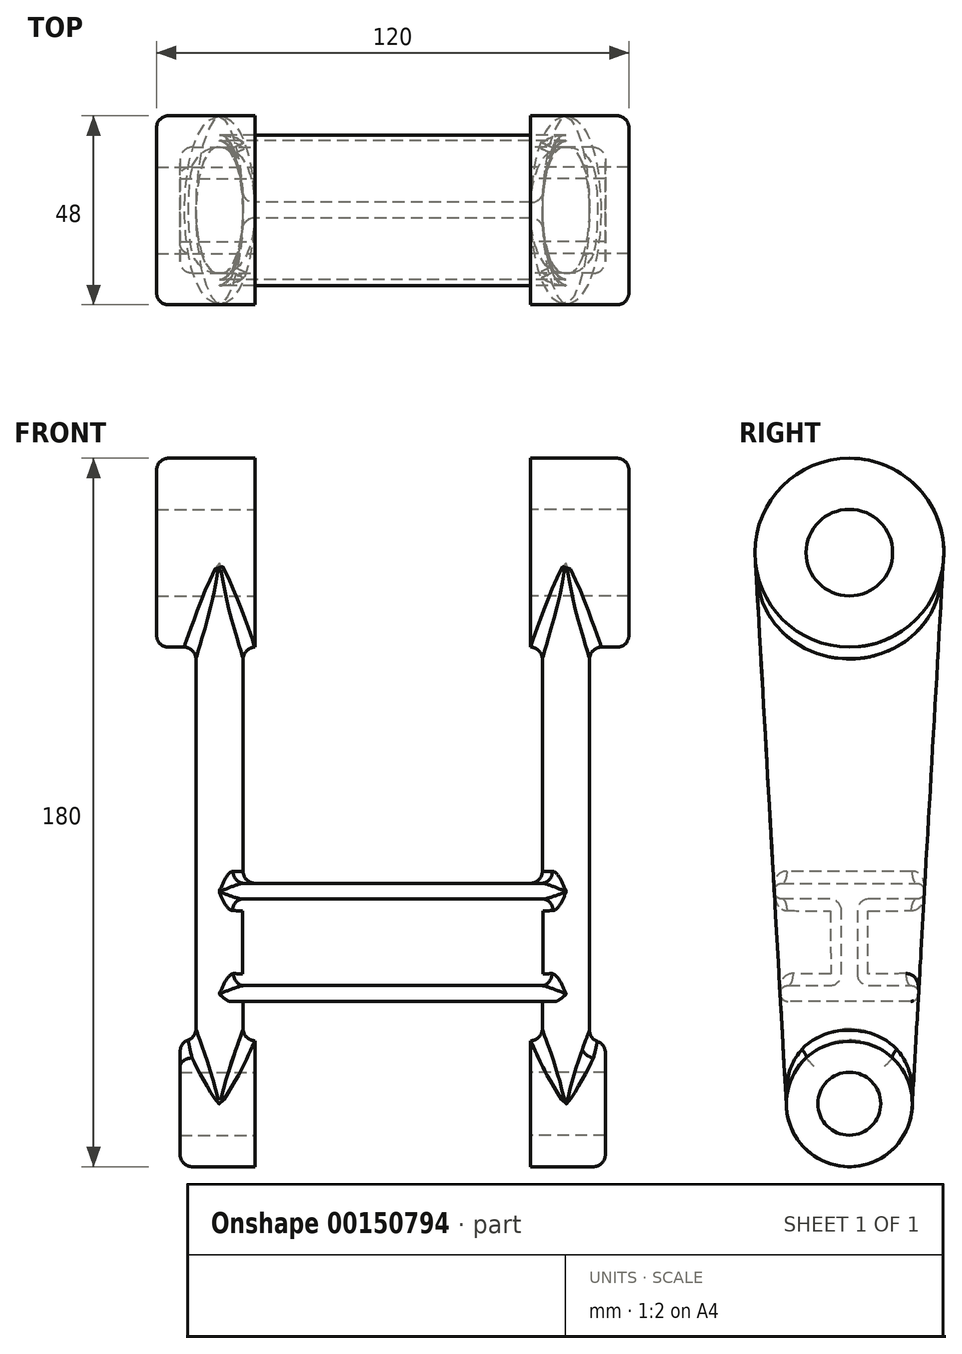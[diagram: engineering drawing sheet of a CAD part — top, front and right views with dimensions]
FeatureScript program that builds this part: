
annotation { "Feature Type Name" : "Feature", "Feature Type Description" : "" }
export const myFeature = defineFeature(function(context is Context, id is Id, definition is map)
    precondition{}
    {
        {
            assignVariable(context, id + "F0", {"name" : "gap", "anyValue" : 70 * mm});
        }
        {
            var Q0;
            Q0=qCreatedBy(makeId("Right.planeOp"),FACE);
            var sketch = newSketch(context, id + "F1", { "sketchPlane" : qUnion([Q0])});
            skCircle(sketch, "E0", {"center": v(0, 0) * mm, "radius": 8 * mm});
            skCircle(sketch, "E1", {"center": v(0, 0) * mm, "radius": 16 * mm});
            skCircle(sketch, "E2", {"center": v(0, 140) * mm, "radius": 11 * mm});
            skCircle(sketch, "E3", {"center": v(0, 140) * mm, "radius": 24 * mm});
            skSolve(sketch);
        }
        {
            var Q0;
            Q0=makeQuery(id+"F1.imprint","IMPRINT",FACE,{"disambiguationData":[TD([[makeQuery(id+"F1.imprint","IMPRINT",EDGE,{"derivedFrom":sQuery(id+"F1.wireOp",EDGE,"E0")}),1.0]])]});
            var Q1;
            Q1=makeQuery(id+"F1.imprint","IMPRINT",FACE,{"disambiguationData":[TD([[makeQuery(id+"F1.imprint","IMPRINT",EDGE,{"derivedFrom":sQuery(id+"F1.wireOp",EDGE,"E0")}),-1.0]])]});
            extrude(context, id + "F2", {"entities" : qUnion([Q0, Q1]), "depth" : 19 * mm});
        }
        {
            var Q0;
            Q0=makeQuery(id+"F1.imprint","IMPRINT",FACE,{"disambiguationData":[TD([[makeQuery(id+"F1.imprint","IMPRINT",EDGE,{"derivedFrom":sQuery(id+"F1.wireOp",EDGE,"E2")}),1.0]])]});
            var Q1;
            Q1=makeQuery(id+"F1.imprint","IMPRINT",FACE,{"disambiguationData":[TD([[makeQuery(id+"F1.imprint","IMPRINT",EDGE,{"derivedFrom":sQuery(id+"F1.wireOp",EDGE,"E2")}),-1.0]])]});
            extrude(context, id + "F3", {"entities" : qUnion([Q0, Q1]), "depth" : 25 * mm});
        }
        {
            var Q0;
            Q0=qCreatedBy(makeId("Top.planeOp"),FACE);
            var sketch = newSketch(context, id + "F4", { "sketchPlane" : qUnion([Q0])});
            skEllipse(sketch, "E4", {"center": v(9, 0) * mm, "majorRadius": 16 * mm, "minorRadius": 6 * mm, "majorAxis": v(0, -1)});
            skPoint(sketch, "E5", {"position": v(3, 0) * mm});
            skLineSegment(sketch, "E6", {"start": v(0, 16) * mm, "end": v(19, 16) * mm, "construction": true});
            skSolve(sketch);
        }
        {
            var Q0;
            Q0=sQuery(id+"F1.wireOp",VERTEX,"E3.center");
            var Q1;
            Q1=qCreatedBy(makeId("Top.planeOp"),FACE);
            cPlane(context, id + "F5", {"entities" : qUnion([Q0, Q1]), "cplaneType" : CPlaneType.PLANE_POINT, "offset" : 25 * mm, "width" : 150 * mm, "height" : 150 * mm});
        }
        {
            var Q0;
            Q0=qCreatedBy(id+"F5.planeOp",FACE);
            var sketch = newSketch(context, id + "F6", { "sketchPlane" : qUnion([Q0])});
            skEllipse(sketch, "E7", {"center": v(9, 0) * mm, "majorRadius": 24 * mm, "minorRadius": 6 * mm, "majorAxis": v(0, 1)});
            skPoint(sketch, "E8", {"position": v(3, 0) * mm});
            skLineSegment(sketch, "E9", {"start": v(0, 24) * mm, "end": v(25, 24) * mm, "construction": true});
            skSolve(sketch);
        }
        {
            var Q0;
            Q0=makeQuery(id+"F6.imprint","IMPRINT",FACE,{"disambiguationData":[TD([[makeQuery(id+"F6.imprint","IMPRINT",EDGE,{"derivedFrom":sQuery(id+"F6.wireOp",EDGE,"E7")}),1.0]])]});
            var Q1;
            Q1=makeQuery(id+"F4.imprint","IMPRINT",FACE,{"disambiguationData":[TD([[makeQuery(id+"F4.imprint","IMPRINT",EDGE,{"derivedFrom":sQuery(id+"F4.wireOp",EDGE,"E4")}),1.0]])]});
            loft(context, id + "F7", {"operationType" : NewBodyOperationType.ADD, "sheetProfilesArray" : [{ "sheetProfileEntities" : qUnion([Q0]) }, { "sheetProfileEntities" : qUnion([Q1]) }]});
        }
        {
            var Q0;
            Q0=makeQuery(id+"F1.imprint","IMPRINT",FACE,{"disambiguationData":[TD([[makeQuery(id+"F1.imprint","IMPRINT",EDGE,{"derivedFrom":sQuery(id+"F1.wireOp",EDGE,"E2")}),1.0]])]});
            var Q1;
            Q1=makeQuery(id+"F1.imprint","IMPRINT",FACE,{"disambiguationData":[TD([[makeQuery(id+"F1.imprint","IMPRINT",EDGE,{"derivedFrom":sQuery(id+"F1.wireOp",EDGE,"E0")}),1.0]])]});
            extrude(context, id + "F8", {"entities" : qUnion([Q0, Q1]), "operationType" : NewBodyOperationType.REMOVE, "depth" : 25 * mm});
        }
        {
            var Q0;
            Q0=sQuery(id+"F4.wireOp",VERTEX,"E4.center");
            var Q1;
            Q1=qCreatedBy(makeId("Right.planeOp"),FACE);
            cPlane(context, id + "F9", {"entities" : qUnion([Q0, Q1]), "cplaneType" : CPlaneType.PLANE_POINT, "offset" : 25 * mm, "width" : 150 * mm, "height" : 150 * mm});
        }
        {
            var Q0;
            Q0=qCreatedBy(makeId("Right.planeOp"),FACE);
            cPlane(context, id + "F10", {"entities" : qUnion([Q0]), "cplaneType" : CPlaneType.OFFSET, "offset" : getVariable(context, 'gap') / 2, "oppositeDirection" : true, "width" : 150 * mm, "height" : 150 * mm});
        }
        {
            var Q0;
            Q0=makeQuery(id+"F2.opExtrude","SWEPT_BODY",BODY,{"disambiguationData":[OSD([sQuery(id+"F1.wireOp",EDGE,"E1")])]});
            var Q1;
            Q1=qCreatedBy(id+"F10.planeOp",FACE);
            mirror(context, id + "F11", {"entities" : qUnion([Q0]), "mirrorPlane" : qUnion([Q1])});
        }
        {
            var Q0;
            Q0=qCreatedBy(makeId("Right.planeOp"),FACE);
            var sketch = newSketch(context, id + "F12", { "sketchPlane" : qUnion([Q0])});
            skLineSegment(sketch, "E10", {"start": v(23.96, 138.63) * mm, "end": v(15.97, -0.91) * mm, "construction": true});
            skLineSegment(sketch, "E11", {"start": v(17.51, 26) * mm, "end": v(-15.6, 26) * mm});
            skLineSegment(sketch, "E12", {"start": v(-15.6, 26) * mm, "end": v(-15.6, 30) * mm, "construction": true});
            skLineSegment(sketch, "E13", {"start": v(-15.6, 30) * mm, "end": v(-5, 30) * mm});
            skLineSegment(sketch, "E14", {"start": v(-2, 33) * mm, "end": v(-2, 49) * mm});
            skLineSegment(sketch, "E15", {"start": v(-5, 52) * mm, "end": v(-17.1, 52) * mm});
            skLineSegment(sketch, "E16", {"start": v(-17.1, 52) * mm, "end": v(-17.1, 56) * mm, "construction": true});
            skLineSegment(sketch, "E17", {"start": v(-17.1, 56) * mm, "end": v(17.11, 56) * mm});
            skLineSegment(sketch, "E18", {"start": v(17.11, 52) * mm, "end": v(5, 52) * mm});
            skLineSegment(sketch, "E19", {"start": v(2, 49) * mm, "end": v(2, 33) * mm});
            skLineSegment(sketch, "E20", {"start": v(5, 30) * mm, "end": v(17.74, 30) * mm});
            skLineSegment(sketch, "E21", {"start": v(15.63, 30) * mm, "end": v(15.63, 26) * mm, "construction": true});
            skLineSegment(sketch, "E22", {"start": v(-23.96, 138.62) * mm, "end": v(-16, 0) * mm, "construction": true});
            skPoint(sketch, "E23.visualSharp", {"position": v(0, 52) * mm});
            skArc(sketch, "E23.filletArc", {"start": v(5, 52) * mm, "mid": v(2.88, 51.12) * mm, "end": v(2, 49) * mm});
            skPoint(sketch, "E24.visualSharp", {"position": v(-2, 52) * mm});
            skArc(sketch, "E24.filletArc", {"start": v(-2, 49) * mm, "mid": v(-2.88, 51.12) * mm, "end": v(-5, 52) * mm});
            skPoint(sketch, "E25.visualSharp", {"position": v(-2, 30) * mm});
            skArc(sketch, "E25.filletArc", {"start": v(-5, 30) * mm, "mid": v(-2.88, 30.88) * mm, "end": v(-2, 33) * mm});
            skPoint(sketch, "E26.visualSharp", {"position": v(2, 30) * mm});
            skArc(sketch, "E26.filletArc", {"start": v(2, 33) * mm, "mid": v(2.88, 30.88) * mm, "end": v(5, 30) * mm});
            skPoint(sketch, "E27.endSnap0", {"position": v(0, 56) * mm});
            skLineSegment(sketch, "E28", {"start": v(0, 0) * mm, "end": v(0, 93.69) * mm, "construction": true});
            skArc(sketch, "E29", {"start": v(-15.6, 30) * mm, "mid": v(-17.6, 28) * mm, "end": v(-15.6, 26) * mm});
            skArc(sketch, "E30", {"start": v(-17.1, 56) * mm, "mid": v(-19.1, 54) * mm, "end": v(-17.1, 52) * mm});
            skArc(sketch, "E31", {"start": v(17.11, 52) * mm, "mid": v(19.11, 54) * mm, "end": v(17.11, 56) * mm});
            skLineSegment(sketch, "E32", {"start": v(17.11, 52) * mm, "end": v(17.11, 56) * mm, "construction": true});
            skArc(sketch, "E33", {"start": v(15.63, 26) * mm, "mid": v(17.63, 28) * mm, "end": v(15.63, 30) * mm});
            skSolve(sketch);
        }
        {
            var Q0;
            Q0=qSketchRegion(id+"F12",true);
            var Q1;
            Q1=qCreatedBy(id+"F9.planeOp",FACE);
            var Q2;
            Q2=qCreatedBy(id+"F10.planeOp",FACE);
            var Q3;
            Q3=makeQuery(id+"F11.opPattern","COPY",BODY,{"derivedFrom":makeQuery(id+"F2.opExtrude","SWEPT_BODY",BODY,{"disambiguationData":[OSD([sQuery(id+"F1.wireOp",EDGE,"E1")])]}),"instanceName":"1"});
            extrude(context, id + "F13", {"entities" : qUnion([Q0]), "operationType" : NewBodyOperationType.ADD, "endBound" : BoundingType.UP_TO_SURFACE, "endBoundEntityFace" : qUnion([Q1]), "depth" : 30 * mm, "hasSecondDirection" : true, "secondDirectionBound" : SecondDirectionBoundingType.UP_TO_SURFACE, "secondDirectionOppositeDirection" : true, "secondDirectionBoundEntityFace" : qUnion([Q2]), "secondDirectionBoundEntityBody" : qUnion([Q3]), "secondDirectionDepth" : 25 * mm});
        }
        {
            var Q0;
            Q0=makeQuery(id+"F13.boolean.opBoolean","INTERSECT",EDGE,{"derivedFrom":[makeQuery(id+"F7.opLoft","SWEPT_FACE",FACE,{"disambiguationData":[OSD([sQuery(id+"F4.wireOp",EDGE,"E4"),sQuery(id+"F6.wireOp",EDGE,"E7")])]}),makeQuery(id+"F13.opExtrude","SWEPT_FACE",FACE,{"disambiguationData":[OSD([sQuery(id+"F12.wireOp",EDGE,"E17")])]})]});
            fillet(context, id + "F14", {"entities" : qUnion([Q0]), "radius" : 3 * mm, "tangentPropagation" : true, "allowEdgeOverflow" : false});
        }
        {
            var Q0;
            Q0=makeQuery(id+"F13.boolean.opBoolean","INTERSECT",EDGE,{"derivedFrom":[makeQuery(id+"F7.opLoft","SWEPT_FACE",FACE,{"disambiguationData":[OSD([sQuery(id+"F4.wireOp",EDGE,"E4"),sQuery(id+"F6.wireOp",EDGE,"E7")])]}),makeQuery(id+"F13.opExtrude","SWEPT_FACE",FACE,{"disambiguationData":[OSD([sQuery(id+"F12.wireOp",EDGE,"E13")])]})]});
            var Q1;
            Q1=makeQuery(id+"F13.boolean.opBoolean","INTERSECT",EDGE,{"derivedFrom":[makeQuery(id+"F7.opLoft","SWEPT_FACE",FACE,{"disambiguationData":[OSD([sQuery(id+"F4.wireOp",EDGE,"E4"),sQuery(id+"F6.wireOp",EDGE,"E7")])]}),makeQuery(id+"F13.opExtrude","SWEPT_FACE",FACE,{"disambiguationData":[OSD([sQuery(id+"F12.wireOp",EDGE,"E14")])]})]});
            var Q2;
            Q2=makeQuery(id+"F13.boolean.opBoolean","INTERSECT",EDGE,{"derivedFrom":[makeQuery(id+"F7.opLoft","SWEPT_FACE",FACE,{"disambiguationData":[OSD([sQuery(id+"F4.wireOp",EDGE,"E4"),sQuery(id+"F6.wireOp",EDGE,"E7")])]}),makeQuery(id+"F13.opExtrude","SWEPT_FACE",FACE,{"disambiguationData":[OSD([sQuery(id+"F12.wireOp",EDGE,"E20")])]})]});
            var Q3;
            Q3=makeQuery(id+"F13.boolean.opBoolean","INTERSECT",EDGE,{"derivedFrom":[makeQuery(id+"F7.opLoft","SWEPT_FACE",FACE,{"disambiguationData":[OSD([sQuery(id+"F4.wireOp",EDGE,"E4"),sQuery(id+"F6.wireOp",EDGE,"E7")])]}),makeQuery(id+"F13.opExtrude","SWEPT_FACE",FACE,{"disambiguationData":[OSD([sQuery(id+"F12.wireOp",EDGE,"E19")])]})]});
            fillet(context, id + "F15", {"entities" : qUnion([Q0, Q1, Q2, Q3]), "radius" : 3 * mm, "tangentPropagation" : true, "allowEdgeOverflow" : false});
        }
        {
            var Q0;
            Q0=makeQuery(id+"F2.opExtrude","SWEPT_BODY",BODY,{"disambiguationData":[OSD([sQuery(id+"F1.wireOp",EDGE,"E1")])]});
            var Q1;
            Q1=qCreatedBy(id+"F10.planeOp",FACE);
            mirror(context, id + "F16", {"operationType" : NewBodyOperationType.ADD, "entities" : qUnion([Q0]), "mirrorPlane" : qUnion([Q1])});
        }
        {
            var Q0;
            Q0=makeQuery(id+"F3.opExtrude","CAP_EDGE",EDGE,{"disambiguationData":[OSD([sQuery(id+"F1.wireOp",EDGE,"E3")])],"isStart":false});
            var Q1;
            Q1=makeQuery(id+"F16.opPattern","COPY",EDGE,{"derivedFrom":makeQuery(id+"F3.opExtrude","CAP_EDGE",EDGE,{"disambiguationData":[OSD([sQuery(id+"F1.wireOp",EDGE,"E3")])],"isStart":false}),"instanceName":"1"});
            var Q2;
            Q2=makeQuery(id+"F2.opExtrude","CAP_EDGE",EDGE,{"disambiguationData":[OSD([sQuery(id+"F1.wireOp",EDGE,"E1")])],"isStart":false});
            var Q3;
            Q3=makeQuery(id+"F16.opPattern","COPY",EDGE,{"derivedFrom":makeQuery(id+"F2.opExtrude","CAP_EDGE",EDGE,{"disambiguationData":[OSD([sQuery(id+"F1.wireOp",EDGE,"E1")])],"isStart":false}),"instanceName":"1"});
            fillet(context, id + "F17", {"entities" : qUnion([Q0, Q1, Q2, Q3]), "radius" : 3 * mm, "tangentPropagation" : true, "allowEdgeOverflow" : false});
        }
        {
            var Q0;
            Q0=makeQuery(id+"F7.boolean.opBoolean","INTERSECT",EDGE,{"derivedFrom":[makeQuery(id+"F3.opExtrude","SWEPT_FACE",FACE,{"disambiguationData":[OSD([sQuery(id+"F1.wireOp",EDGE,"E3")])]}),makeQuery(id+"F7.opLoft","SWEPT_FACE",FACE,{"disambiguationData":[OSD([sQuery(id+"F4.wireOp",EDGE,"E4"),sQuery(id+"F6.wireOp",EDGE,"E7")])]})]});
            var Q1;
            Q1=makeQuery(id+"F11.opPattern","COPY",EDGE,{"derivedFrom":makeQuery(id+"F7.boolean.opBoolean","INTERSECT",EDGE,{"derivedFrom":[makeQuery(id+"F3.opExtrude","SWEPT_FACE",FACE,{"disambiguationData":[OSD([sQuery(id+"F1.wireOp",EDGE,"E3")])]}),makeQuery(id+"F7.opLoft","SWEPT_FACE",FACE,{"disambiguationData":[OSD([sQuery(id+"F4.wireOp",EDGE,"E4"),sQuery(id+"F6.wireOp",EDGE,"E7")])]})]}),"instanceName":"1"});
            var Q2;
            Q2=makeQuery(id+"F11.opPattern","COPY",EDGE,{"derivedFrom":makeQuery(id+"F7.boolean.opBoolean","INTERSECT",EDGE,{"derivedFrom":[makeQuery(id+"F2.opExtrude","SWEPT_FACE",FACE,{"disambiguationData":[OSD([sQuery(id+"F1.wireOp",EDGE,"E1")])]}),makeQuery(id+"F7.opLoft","SWEPT_FACE",FACE,{"disambiguationData":[OSD([sQuery(id+"F4.wireOp",EDGE,"E4"),sQuery(id+"F6.wireOp",EDGE,"E7")])]})]}),"instanceName":"1"});
            var Q3;
            Q3=makeQuery(id+"F7.boolean.opBoolean","INTERSECT",EDGE,{"derivedFrom":[makeQuery(id+"F2.opExtrude","SWEPT_FACE",FACE,{"disambiguationData":[OSD([sQuery(id+"F1.wireOp",EDGE,"E1")])]}),makeQuery(id+"F7.opLoft","SWEPT_FACE",FACE,{"disambiguationData":[OSD([sQuery(id+"F4.wireOp",EDGE,"E4"),sQuery(id+"F6.wireOp",EDGE,"E7")])]})]});
            fillet(context, id + "F18", {"entities" : qUnion([Q0, Q1, Q2, Q3]), "radius" : 3 * mm, "tangentPropagation" : true, "allowEdgeOverflow" : false});
        }
        {
            var Q0;
            Q0=makeQuery(id+"F11.opPattern","COPY",EDGE,{"derivedFrom":makeQuery(id+"F2.opExtrude","CAP_EDGE",EDGE,{"disambiguationData":[OSD([sQuery(id+"F1.wireOp",EDGE,"E1")])],"isStart":false}),"instanceName":"1"});
            var Q1;
            Q1=makeQuery(id+"F11.opPattern","COPY",EDGE,{"derivedFrom":makeQuery(id+"F3.opExtrude","CAP_EDGE",EDGE,{"disambiguationData":[OSD([sQuery(id+"F1.wireOp",EDGE,"E3")])],"isStart":false}),"instanceName":"1"});
            fillet(context, id + "F19", {"entities" : qUnion([Q0, Q1]), "radius" : 3 * mm, "tangentPropagation" : true, "allowEdgeOverflow" : false});
        }
    });
